# Revit family: Насосно-смесительные модули ECO2 MK
name_source: partatom
category: Арматура трубопроводов
units: mm (PartAtom-declared; Revit-internal decimal feet)

## family parameters
Всегда вертикально = Да
На основе рабочей плоскости = Нет
Общий = Да
При загрузке вырезать с полостями = Нет
Размер круглого соединителя = Использовать диаметр
Тип детали = Встроенный датчик

## types (2) — shared parameters
ADSK_Единица измерения = шт.
ADSK_Завод-изготовитель = HuchEnTEC
ADSK_Марка = HuchEnTEC ECO2
HYBRID = Да
UPS = Да
Изготовитель = HuchEnTEC
Описание = Насосная группа, ECO2 MK 32
zero-valued in all types: Отметка по умолчанию

## per-type parameters (varying)
| type | ADSK_Код изделия | ADSK_Наименование краткое | Kvs | PN | Qmax | ΔТ1 | ΔТ2 | ВР | НР |
| ECO 2 MK DN25 | 101.35.025 | Насосная группа, ECO2 MK 25 | 6.1 | 600000.0 Па | 48000 Вт | 20 °C | 10 °C | 25 мм | 40 мм |
| ECO 2 MK DN32 | 101.35.032 | Насосная группа, ECO2 MK 32 | 16 | 1000000.0 Па | 76000 Вт | 15 °C | 0 °C | 32 мм | 50 мм |

## geometry (parser evidence)
native form markers: Sweep x6
no freeform markers — native parametric forms only
